# Revit family: Remote_Chiller_Non-Filtered -Elkay-ER101Y
name_source: partatom
category: Plumbing Fixtures
units: mm (PartAtom-declared; Revit-internal decimal feet)

## family parameters
Always vertical = Yes
Cut with Voids When Loaded = No
Maintain Annotation Orientation = No
OmniClass Number = 23.45.05.14.14
OmniClass Title = Sinks/Lavatories
Part Type = Normal
Room Calculation Point = No
Round Connector Dimension = Use Diameter
Shared = No
Work Plane-Based = No

## types (1)
- ER101Y (Remote Chiller)
    Approx. Shipping Weight (lbs) = 74
    Assembly Code = D2010800
    Chilling Capacity(GPH) = 10
    Default Elevation = 0.000"
    Description = Remote Chiller Non-Filtered Refrigerated 10 GPH
    Dimensions = 19 1/2 inch x 7 7/8 inch x 22 inch
    Height = 22.000"
    Inlet Connection Size (inch) = 0.375"
    Installation Location = Indoor
    Length = 19.500"
    Main Material = Finish-Elkay-Galvanized steel
    Manufacturer = Elkay Manufacturer Company
    Manufacturer Brand = Elkay (by Zurn Elkay Water Solutions)
    Model = ER101Y
    Outlet Connection Size (inch) = 0.375"
    Product Documentation Link = https://www.elkayfiles.com
    Product Installation Sheet URL = https://www.elkayfiles.com
    Product Page URL = https://www.elkay.com
    Product Weight (lbs) = 68
    Product data URL = https://www.bimobject.com
    Repair Parts URL = https://www.elkayfiles.com
    Type Image = <None>
    URL = https://www.elkay.com
    Voltage = 115 V
    Width = 7.875"

## geometry (parser evidence)
native form markers: Sweep x2
no freeform markers — native parametric forms only
